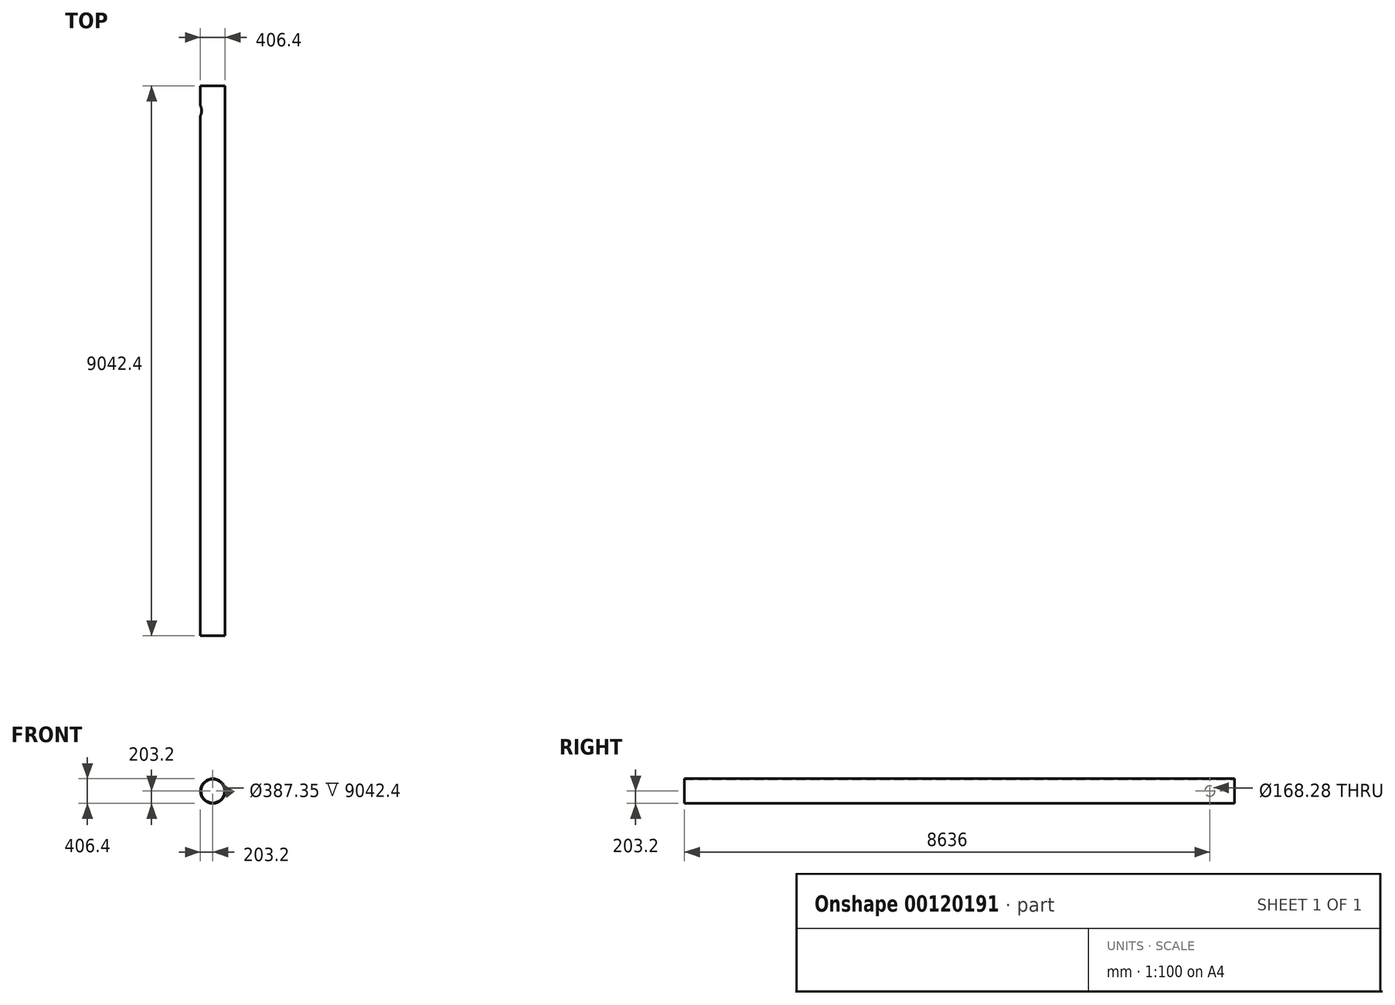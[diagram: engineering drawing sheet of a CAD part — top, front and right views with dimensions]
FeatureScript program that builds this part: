
annotation { "Feature Type Name" : "Feature", "Feature Type Description" : "" }
export const myFeature = defineFeature(function(context is Context, id is Id, definition is map)
    precondition{}
    {
        {
            var Q0;
            Q0=qCreatedBy(makeId("Front.planeOp"),FACE);
            var sketch = newSketch(context, id + "F0", { "sketchPlane" : qUnion([Q0])});
            skCircle(sketch, "E0", {"center": v(0, 0) * mm, "radius": 203.2 * mm});
            skCircle(sketch, "E1", {"center": v(0, 0) * mm, "radius": 193.68 * mm});
            skSolve(sketch);
        }
        {
            var Q0;
            Q0 = qSketchRegion(id + "F0", true);
            extrude(context, id + "F1", {"entities" : qUnion([Q0]), "depth" : 9042.4 * mm});
        }
        {
            var Q0;
            Q0=qCreatedBy(makeId("Right.planeOp"),FACE);
            var sketch = newSketch(context, id + "F2", { "sketchPlane" : qUnion([Q0])});
            skCircle(sketch, "E2", {"center": v(-406.4, 0) * mm, "radius": 84.14 * mm});
            skSolve(sketch);
        }
        {
            var Q0;
            Q0 = qSketchRegion(id + "F2", true);
            extrude(context, id + "F3", {"entities" : qUnion([Q0]), "operationType" : NewBodyOperationType.REMOVE, "oppositeDirection" : true, "depth" : 254 * mm});
        }
    });
